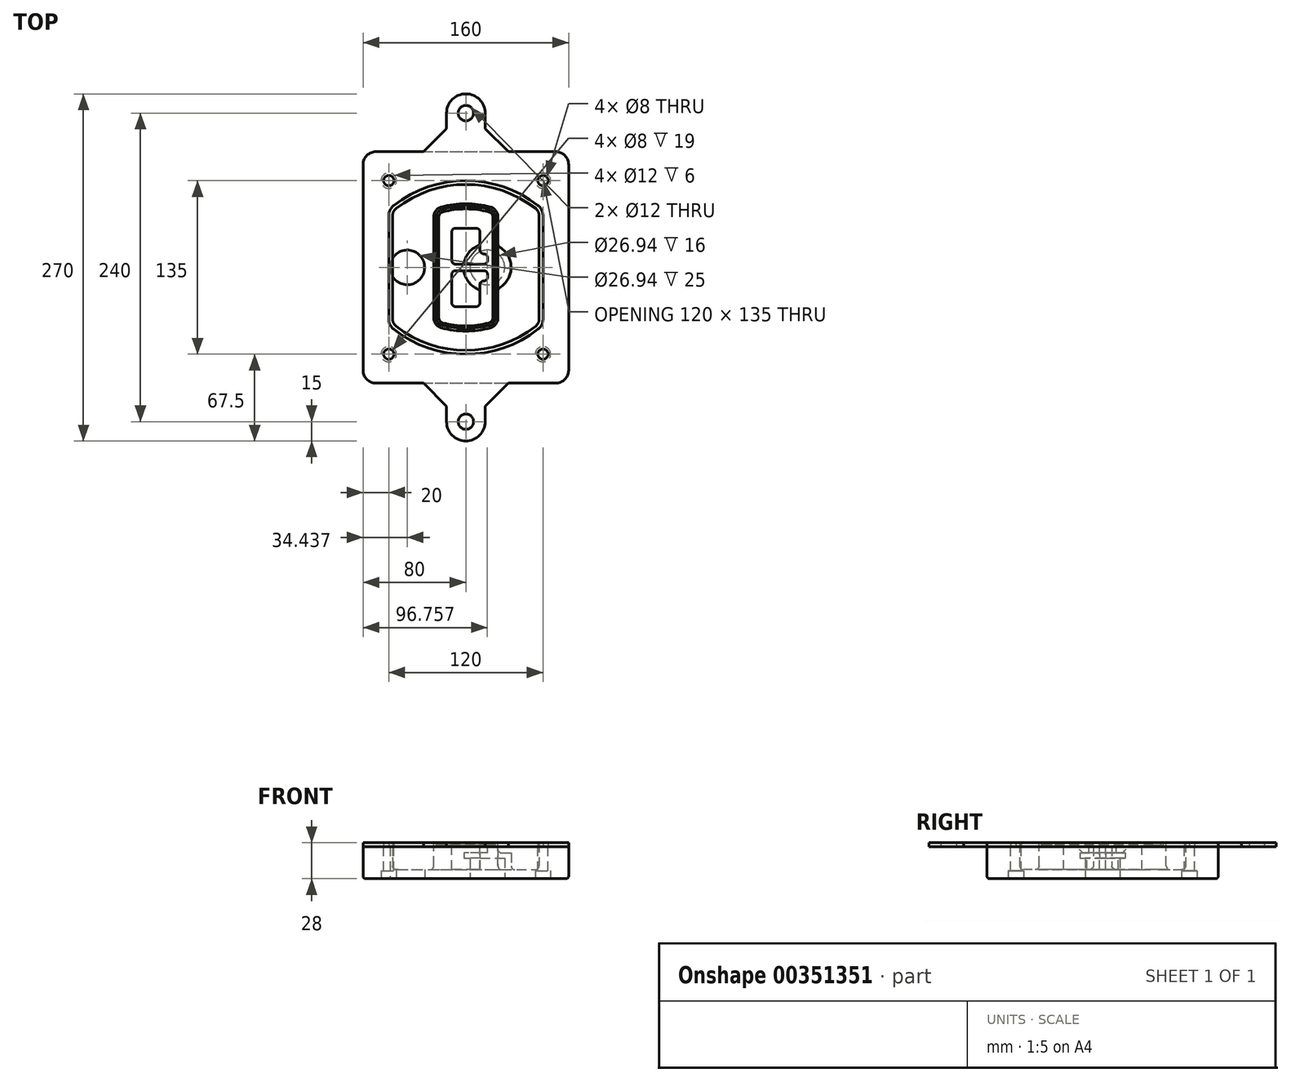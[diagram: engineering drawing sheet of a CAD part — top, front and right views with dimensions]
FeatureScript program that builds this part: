
annotation { "Feature Type Name" : "Feature", "Feature Type Description" : "" }
export const myFeature = defineFeature(function(context is Context, id is Id, definition is map)
    precondition{}
    {
        {
            var Q0;
            Q0=qCreatedBy(makeId("Top.planeOp"),FACE);
            var sketch = newSketch(context, id + "F0", { "sketchPlane" : qUnion([Q0])});
            skPoint(sketch, "E0.rect.middle", {"position": v(0, 0) * mm});
            skLineSegment(sketch, "E1.bottom", {"start": v(-70, -90) * mm, "end": v(70, -90) * mm});
            skLineSegment(sketch, "E1.top", {"start": v(-70, 90) * mm, "end": v(70, 90) * mm});
            skLineSegment(sketch, "E1.left", {"start": v(-80, -80) * mm, "end": v(-80, 80) * mm});
            skLineSegment(sketch, "E1.right", {"start": v(80, -80) * mm, "end": v(80, 80) * mm});
            skLineSegment(sketch, "E2", {"start": v(-80, 90) * mm, "end": v(80, -90) * mm, "construction": true});
            skLineSegment(sketch, "E3", {"start": v(80, 90) * mm, "end": v(-80, -90) * mm, "construction": true});
            skCircle(sketch, "E4", {"center": v(-60, 67.5) * mm, "radius": 4 * mm});
            skCircle(sketch, "E5", {"center": v(60, 67.5) * mm, "radius": 4 * mm});
            skCircle(sketch, "E6", {"center": v(60, -67.5) * mm, "radius": 4 * mm});
            skCircle(sketch, "E7", {"center": v(-60, -67.5) * mm, "radius": 4 * mm});
            skLineSegment(sketch, "E8", {"start": v(-60, 67.5) * mm, "end": v(60, 67.5) * mm, "construction": true});
            skLineSegment(sketch, "E9", {"start": v(60, 67.5) * mm, "end": v(60, -67.5) * mm, "construction": true});
            skLineSegment(sketch, "E10", {"start": v(60, -67.5) * mm, "end": v(-60, -67.5) * mm, "construction": true});
            skLineSegment(sketch, "E11", {"start": v(-60, -67.5) * mm, "end": v(-60, 67.5) * mm, "construction": true});
            skLineSegment(sketch, "E12", {"start": v(-60, 40.3) * mm, "end": v(-60, -40.3) * mm});
            skLineSegment(sketch, "E13", {"start": v(60, 40.3) * mm, "end": v(60, -40.3) * mm});
            skArc(sketch, "E14", {"start": v(56.15, 48.18) * mm, "mid": v(0, 67.5) * mm, "end": v(-56.15, 48.18) * mm});
            skArc(sketch, "E15", {"start": v(-56.15, -48.18) * mm, "mid": v(0, -67.5) * mm, "end": v(56.15, -48.18) * mm});
            skLineSegment(sketch, "E16", {"start": v(-60, 0) * mm, "end": v(60, 0) * mm, "construction": true});
            skPoint(sketch, "E17.visualSharp", {"position": v(-60, -45) * mm});
            skArc(sketch, "E17.filletArc", {"start": v(-60, -40.3) * mm, "mid": v(-58.99, -44.68) * mm, "end": v(-56.15, -48.18) * mm});
            skPoint(sketch, "E18.visualSharp", {"position": v(-60, 45) * mm});
            skArc(sketch, "E18.filletArc", {"start": v(-56.15, 48.18) * mm, "mid": v(-58.99, 44.68) * mm, "end": v(-60, 40.3) * mm});
            skPoint(sketch, "E19.visualSharp", {"position": v(60, 45) * mm});
            skArc(sketch, "E19.filletArc", {"start": v(60, 40.3) * mm, "mid": v(58.99, 44.68) * mm, "end": v(56.15, 48.18) * mm});
            skPoint(sketch, "E20.visualSharp", {"position": v(60, -45) * mm});
            skArc(sketch, "E20.filletArc", {"start": v(56.15, -48.18) * mm, "mid": v(58.99, -44.68) * mm, "end": v(60, -40.3) * mm});
            skPoint(sketch, "E21.visualSharp", {"position": v(-80, 90) * mm});
            skArc(sketch, "E21.filletArc", {"start": v(-70, 90) * mm, "mid": v(-77.07, 87.07) * mm, "end": v(-80, 80) * mm});
            skPoint(sketch, "E22.visualSharp", {"position": v(80, 90) * mm});
            skArc(sketch, "E22.filletArc", {"start": v(80, 80) * mm, "mid": v(77.07, 87.07) * mm, "end": v(70, 90) * mm});
            skPoint(sketch, "E23.visualSharp", {"position": v(80, -90) * mm});
            skArc(sketch, "E23.filletArc", {"start": v(70, -90) * mm, "mid": v(77.07, -87.07) * mm, "end": v(80, -80) * mm});
            skPoint(sketch, "E24.visualSharp", {"position": v(-80, -90) * mm});
            skArc(sketch, "E24.filletArc", {"start": v(-80, -80) * mm, "mid": v(-77.07, -87.07) * mm, "end": v(-70, -90) * mm});
            skArc(sketch, "E25.0", {"start": v(57, 40.3) * mm, "mid": v(56.3, 43.36) * mm, "end": v(54.3, 45.81) * mm});
            skLineSegment(sketch, "E25.1", {"start": v(57, 40.3) * mm, "end": v(57, -40.3) * mm});
            skArc(sketch, "E25.2", {"start": v(54.3, -45.81) * mm, "mid": v(56.3, -43.36) * mm, "end": v(57, -40.3) * mm});
            skArc(sketch, "E25.3", {"start": v(-54.3, -45.81) * mm, "mid": v(0, -64.5) * mm, "end": v(54.3, -45.81) * mm});
            skArc(sketch, "E25.4", {"start": v(-57, -40.3) * mm, "mid": v(-56.3, -43.36) * mm, "end": v(-54.3, -45.81) * mm});
            skArc(sketch, "E25.5", {"start": v(54.3, 45.81) * mm, "mid": v(0, 64.5) * mm, "end": v(-54.3, 45.81) * mm});
            skLineSegment(sketch, "E25.6", {"start": v(-57, 40.3) * mm, "end": v(-57, -40.3) * mm});
            skArc(sketch, "E25.7", {"start": v(-54.3, 45.81) * mm, "mid": v(-56.3, 43.36) * mm, "end": v(-57, 40.3) * mm});
            skArc(sketch, "E26.0", {"start": v(-58.62, 51.33) * mm, "mid": v(-62.58, 46.43) * mm, "end": v(-64, 40.3) * mm});
            skArc(sketch, "E26.1", {"start": v(58.62, 51.33) * mm, "mid": v(0, 71.5) * mm, "end": v(-58.62, 51.33) * mm});
            skArc(sketch, "E26.2", {"start": v(64, 40.3) * mm, "mid": v(62.58, 46.43) * mm, "end": v(58.62, 51.33) * mm});
            skLineSegment(sketch, "E26.3", {"start": v(64, 40.3) * mm, "end": v(64, -40.3) * mm});
            skArc(sketch, "E26.4", {"start": v(58.62, -51.33) * mm, "mid": v(62.58, -46.43) * mm, "end": v(64, -40.3) * mm});
            skLineSegment(sketch, "E26.5", {"start": v(-64, 40.3) * mm, "end": v(-64, -40.3) * mm});
            skArc(sketch, "E26.6", {"start": v(-58.62, -51.33) * mm, "mid": v(0, -71.5) * mm, "end": v(58.62, -51.33) * mm});
            skArc(sketch, "E26.7", {"start": v(-64, -40.3) * mm, "mid": v(-62.58, -46.43) * mm, "end": v(-58.62, -51.33) * mm});
            skSolve(sketch);
        }
        {
            var Q0;
            Q0=makeQuery(id+"F0.imprint","IMPRINT",FACE,{"disambiguationData":[TD([[makeQuery(id+"F0.imprint","IMPRINT",EDGE,{"derivedFrom":sQuery(id+"F0.wireOp",EDGE,"E1.bottom")}),1.0]])]});
            var Q1;
            Q1=makeQuery(id+"F0.imprint","IMPRINT",FACE,{"disambiguationData":[TD([[makeQuery(id+"F0.imprint","IMPRINT",EDGE,{"derivedFrom":sQuery(id+"F0.wireOp",EDGE,"E12")}),1.0]])]});
            var Q2;
            Q2=makeQuery(id+"F0.imprint","IMPRINT",FACE,{"disambiguationData":[TD([[makeQuery(id+"F0.imprint","IMPRINT",EDGE,{"derivedFrom":sQuery(id+"F0.wireOp",EDGE,"E25.0")}),1.0]])]});
            var Q3;
            Q3=makeQuery(id+"F0.imprint","IMPRINT",FACE,{"disambiguationData":[TD([[makeQuery(id+"F0.imprint","IMPRINT",EDGE,{"derivedFrom":sQuery(id+"F0.wireOp",EDGE,"E12")}),-1.0]])]});
            extrude(context, id + "F1", {"entities" : qUnion([Q0, Q1, Q2, Q3]), "oppositeDirection" : true, "depth" : 25 * mm});
        }
        {
            var Q0;
            Q0=makeQuery(id+"F0.imprint","IMPRINT",FACE,{"disambiguationData":[TD([[makeQuery(id+"F0.imprint","IMPRINT",EDGE,{"derivedFrom":sQuery(id+"F0.wireOp",EDGE,"E12")}),1.0]])]});
            extrude(context, id + "F2", {"entities" : qUnion([Q0]), "operationType" : NewBodyOperationType.ADD, "depth" : 3 * mm});
        }
        {
            var Q0;
            Q0=makeQuery(id+"F0.imprint","IMPRINT",FACE,{"disambiguationData":[TD([[makeQuery(id+"F0.imprint","IMPRINT",EDGE,{"derivedFrom":sQuery(id+"F0.wireOp",EDGE,"E25.0")}),1.0]])]});
            extrude(context, id + "F3", {"entities" : qUnion([Q0]), "operationType" : NewBodyOperationType.REMOVE, "oppositeDirection" : true, "depth" : 18 * mm});
        }
        {
            var Q0;
            Q0=makeQuery(id+"F2.opExtrude","CAP_FACE",FACE,{"disambiguationData":[OSD([sQuery(id+"F0.wireOp",EDGE,"E12"),sQuery(id+"F0.wireOp",EDGE,"E13"),sQuery(id+"F0.wireOp",EDGE,"E14"),sQuery(id+"F0.wireOp",EDGE,"E15"),sQuery(id+"F0.wireOp",EDGE,"E17.filletArc"),sQuery(id+"F0.wireOp",EDGE,"E18.filletArc"),sQuery(id+"F0.wireOp",EDGE,"E19.filletArc"),sQuery(id+"F0.wireOp",EDGE,"E20.filletArc"),sQuery(id+"F0.wireOp",EDGE,"E25.0"),sQuery(id+"F0.wireOp",EDGE,"E25.1"),sQuery(id+"F0.wireOp",EDGE,"E25.2"),sQuery(id+"F0.wireOp",EDGE,"E25.3"),sQuery(id+"F0.wireOp",EDGE,"E25.4"),sQuery(id+"F0.wireOp",EDGE,"E25.5"),sQuery(id+"F0.wireOp",EDGE,"E25.6"),sQuery(id+"F0.wireOp",EDGE,"E25.7")])],"isStart":false});
            var sketch = newSketch(context, id + "F4", { "sketchPlane" : qUnion([Q0])});
            skArc(sketch, "E27.0", {"start": v(-19.08, -46.97) * mm, "mid": v(0, -49.5) * mm, "end": v(19.08, -46.97) * mm});
            skArc(sketch, "E28.0", {"start": v(19.08, 46.97) * mm, "mid": v(0, 49.5) * mm, "end": v(-19.08, 46.97) * mm});
            skLineSegment(sketch, "E29", {"start": v(-25, 39.25) * mm, "end": v(-25, -39.25) * mm});
            skLineSegment(sketch, "E30", {"start": v(25, 39.25) * mm, "end": v(25, -39.25) * mm});
            skLineSegment(sketch, "E31", {"start": v(-25, 45.1) * mm, "end": v(25, 45.1) * mm, "construction": true});
            skLineSegment(sketch, "E32", {"start": v(-25, -45.1) * mm, "end": v(25, -45.1) * mm, "construction": true});
            skPoint(sketch, "E33.visualSharp", {"position": v(-25, 45.1) * mm});
            skArc(sketch, "E33.filletArc", {"start": v(-19.08, 46.97) * mm, "mid": v(-23.35, 44.11) * mm, "end": v(-25, 39.25) * mm});
            skPoint(sketch, "E34.visualSharp", {"position": v(25, 45.1) * mm});
            skArc(sketch, "E34.filletArc", {"start": v(25, 39.25) * mm, "mid": v(23.35, 44.11) * mm, "end": v(19.08, 46.97) * mm});
            skPoint(sketch, "E35.visualSharp", {"position": v(25, -45.1) * mm});
            skArc(sketch, "E35.filletArc", {"start": v(19.08, -46.97) * mm, "mid": v(23.35, -44.11) * mm, "end": v(25, -39.25) * mm});
            skPoint(sketch, "E36.visualSharp", {"position": v(-25, -45.1) * mm});
            skArc(sketch, "E36.filletArc", {"start": v(-25, -39.25) * mm, "mid": v(-23.35, -44.11) * mm, "end": v(-19.08, -46.97) * mm});
            skArc(sketch, "E37.0", {"start": v(54.3, 45.81) * mm, "mid": v(0, 64.5) * mm, "end": v(-54.3, 45.81) * mm});
            skArc(sketch, "E37.1", {"start": v(-54.3, 45.81) * mm, "mid": v(-56.3, 43.36) * mm, "end": v(-57, 40.3) * mm});
            skLineSegment(sketch, "E37.2", {"start": v(-57, 40.3) * mm, "end": v(-57, -40.3) * mm});
            skArc(sketch, "E37.3", {"start": v(-57, -40.3) * mm, "mid": v(-56.3, -43.36) * mm, "end": v(-54.3, -45.81) * mm});
            skArc(sketch, "E37.4", {"start": v(-54.3, -45.81) * mm, "mid": v(0, -64.5) * mm, "end": v(54.3, -45.81) * mm});
            skArc(sketch, "E37.5", {"start": v(54.3, -45.81) * mm, "mid": v(56.3, -43.36) * mm, "end": v(57, -40.3) * mm});
            skLineSegment(sketch, "E37.6", {"start": v(57, 40.3) * mm, "end": v(57, -40.3) * mm});
            skArc(sketch, "E37.7", {"start": v(57, 40.3) * mm, "mid": v(56.3, 43.36) * mm, "end": v(54.3, 45.81) * mm});
            skLineSegment(sketch, "E38.0", {"start": v(23, 39.25) * mm, "end": v(23, -39.25) * mm});
            skArc(sketch, "E38.1", {"start": v(18.56, -45.04) * mm, "mid": v(21.76, -42.9) * mm, "end": v(23, -39.25) * mm});
            skArc(sketch, "E38.2", {"start": v(-18.56, -45.04) * mm, "mid": v(0, -47.5) * mm, "end": v(18.56, -45.04) * mm});
            skArc(sketch, "E38.3", {"start": v(-23, -39.25) * mm, "mid": v(-21.76, -42.9) * mm, "end": v(-18.56, -45.04) * mm});
            skLineSegment(sketch, "E38.4", {"start": v(-23, 39.25) * mm, "end": v(-23, -39.25) * mm});
            skArc(sketch, "E38.5", {"start": v(23, 39.25) * mm, "mid": v(21.76, 42.9) * mm, "end": v(18.56, 45.04) * mm});
            skArc(sketch, "E38.6", {"start": v(-18.56, 45.04) * mm, "mid": v(-21.76, 42.9) * mm, "end": v(-23, 39.25) * mm});
            skArc(sketch, "E38.7", {"start": v(18.56, 45.04) * mm, "mid": v(0, 47.5) * mm, "end": v(-18.56, 45.04) * mm});
            skArc(sketch, "E39.0", {"start": v(21, 39.25) * mm, "mid": v(20.18, 41.68) * mm, "end": v(18.04, 43.1) * mm});
            skLineSegment(sketch, "E39.1", {"start": v(21, 39.25) * mm, "end": v(21, -39.25) * mm});
            skArc(sketch, "E39.2", {"start": v(18.04, -43.1) * mm, "mid": v(20.18, -41.68) * mm, "end": v(21, -39.25) * mm});
            skArc(sketch, "E39.3", {"start": v(-18.04, -43.1) * mm, "mid": v(0, -45.5) * mm, "end": v(18.04, -43.1) * mm});
            skArc(sketch, "E39.4", {"start": v(-21, -39.25) * mm, "mid": v(-20.18, -41.68) * mm, "end": v(-18.04, -43.1) * mm});
            skArc(sketch, "E39.5", {"start": v(18.04, 43.1) * mm, "mid": v(0, 45.5) * mm, "end": v(-18.04, 43.1) * mm});
            skLineSegment(sketch, "E39.6", {"start": v(-21, 39.25) * mm, "end": v(-21, -39.25) * mm});
            skArc(sketch, "E39.7", {"start": v(-18.04, 43.1) * mm, "mid": v(-20.18, 41.68) * mm, "end": v(-21, 39.25) * mm});
            skLineSegment(sketch, "E40", {"start": v(-25, 0) * mm, "end": v(25, 0) * mm, "construction": true});
            skLineSegment(sketch, "E41", {"start": v(-11, 5.5) * mm, "end": v(-11, 27.5) * mm});
            skLineSegment(sketch, "E42", {"start": v(-8, 30.5) * mm, "end": v(8, 30.5) * mm});
            skLineSegment(sketch, "E43", {"start": v(11, 27.5) * mm, "end": v(11, 13.5) * mm});
            skLineSegment(sketch, "E44", {"start": v(14, 10.5) * mm, "end": v(14, 10.5) * mm});
            skLineSegment(sketch, "E45", {"start": v(17, 7.5) * mm, "end": v(17, 5.5) * mm});
            skLineSegment(sketch, "E46", {"start": v(14, 2.5) * mm, "end": v(-8, 2.5) * mm});
            skPoint(sketch, "E47.visualSharp", {"position": v(-11, 30.5) * mm});
            skArc(sketch, "E47.filletArc", {"start": v(-8, 30.5) * mm, "mid": v(-10.12, 29.62) * mm, "end": v(-11, 27.5) * mm});
            skPoint(sketch, "E48.visualSharp", {"position": v(11, 30.5) * mm});
            skArc(sketch, "E48.filletArc", {"start": v(11, 27.5) * mm, "mid": v(10.12, 29.62) * mm, "end": v(8, 30.5) * mm});
            skPoint(sketch, "E49.visualSharp", {"position": v(11, 10.5) * mm});
            skArc(sketch, "E49.filletArc", {"start": v(11, 13.5) * mm, "mid": v(11.88, 11.38) * mm, "end": v(14, 10.5) * mm});
            skPoint(sketch, "E50.visualSharp", {"position": v(17, 10.5) * mm});
            skArc(sketch, "E50.filletArc", {"start": v(17, 7.5) * mm, "mid": v(16.12, 9.62) * mm, "end": v(14, 10.5) * mm});
            skPoint(sketch, "E51.visualSharp", {"position": v(17, 2.5) * mm});
            skArc(sketch, "E51.filletArc", {"start": v(14, 2.5) * mm, "mid": v(16.12, 3.38) * mm, "end": v(17, 5.5) * mm});
            skPoint(sketch, "E52.visualSharp", {"position": v(-11, 2.5) * mm});
            skArc(sketch, "E52.filletArc", {"start": v(-11, 5.5) * mm, "mid": v(-10.12, 3.38) * mm, "end": v(-8, 2.5) * mm});
            skLineSegment(sketch, "E53.0.MirrorCS", {"start": v(14, -2.5) * mm, "end": v(-8, -2.5) * mm});
            skArc(sketch, "E54.0.MirrorCS", {"start": v(-11, -5.5) * mm, "mid": v(-10.12, -3.38) * mm, "end": v(-8, -2.5) * mm});
            skLineSegment(sketch, "E55.0.MirrorCS", {"start": v(-11, -5.5) * mm, "end": v(-11, -27.5) * mm});
            skArc(sketch, "E56.0.MirrorCS", {"start": v(-8, -30.5) * mm, "mid": v(-10.12, -29.62) * mm, "end": v(-11, -27.5) * mm});
            skLineSegment(sketch, "E57.0.MirrorCS", {"start": v(-8, -30.5) * mm, "end": v(8, -30.5) * mm});
            skArc(sketch, "E58.0.MirrorCS", {"start": v(11, -27.5) * mm, "mid": v(10.12, -29.62) * mm, "end": v(8, -30.5) * mm});
            skLineSegment(sketch, "E59.0.MirrorCS", {"start": v(11, -27.5) * mm, "end": v(11, -13.5) * mm});
            skArc(sketch, "E60.0.MirrorCS", {"start": v(11, -13.5) * mm, "mid": v(11.88, -11.38) * mm, "end": v(14, -10.5) * mm});
            skArc(sketch, "E61.0.MirrorCS", {"start": v(17, -7.5) * mm, "mid": v(16.12, -9.62) * mm, "end": v(14, -10.5) * mm});
            skLineSegment(sketch, "E62.0.MirrorCS", {"start": v(17, -7.5) * mm, "end": v(17, -5.5) * mm});
            skArc(sketch, "E63.0.MirrorCS", {"start": v(14, -2.5) * mm, "mid": v(16.12, -3.38) * mm, "end": v(17, -5.5) * mm});
            skSolve(sketch);
        }
        {
            var Q0;
            Q0=makeQuery(id+"F4.imprint","IMPRINT",FACE,{"disambiguationData":[TD([[makeQuery(id+"F4.imprint","IMPRINT",EDGE,{"derivedFrom":sQuery(id+"F4.wireOp",EDGE,"E27.0")}),1.0]])]});
            var Q1;
            Q1=makeQuery(id+"F4.imprint","IMPRINT",FACE,{"disambiguationData":[TD([[makeQuery(id+"F4.imprint","IMPRINT",EDGE,{"derivedFrom":sQuery(id+"F4.wireOp",EDGE,"E38.0")}),-1.0]])]});
            var Q2;
            Q2=makeQuery(id+"F4.imprint","IMPRINT",FACE,{"disambiguationData":[TD([[makeQuery(id+"F4.imprint","IMPRINT",EDGE,{"derivedFrom":sQuery(id+"F4.wireOp",EDGE,"E39.0")}),1.0]])]});
            extrude(context, id + "F5", {"entities" : qUnion([Q0, Q1, Q2]), "operationType" : NewBodyOperationType.ADD, "endBound" : BoundingType.UP_TO_NEXT, "oppositeDirection" : true, "depth" : 25 * mm});
        }
        {
            var Q0;
            Q0=makeQuery(id+"F4.imprint","IMPRINT",FACE,{"disambiguationData":[TD([[makeQuery(id+"F4.imprint","IMPRINT",EDGE,{"derivedFrom":sQuery(id+"F4.wireOp",EDGE,"E38.0")}),-1.0]])]});
            extrude(context, id + "F6", {"entities" : qUnion([Q0]), "operationType" : NewBodyOperationType.REMOVE, "oppositeDirection" : true, "depth" : 2 * mm});
        }
        {
            var Q0;
            Q0=makeQuery(id+"F1.opExtrude","CAP_FACE",FACE,{"disambiguationData":[OSD([sQuery(id+"F0.wireOp",EDGE,"E1.bottom"),sQuery(id+"F0.wireOp",EDGE,"E1.top"),sQuery(id+"F0.wireOp",EDGE,"E1.left"),sQuery(id+"F0.wireOp",EDGE,"E1.right"),sQuery(id+"F0.wireOp",EDGE,"E4"),sQuery(id+"F0.wireOp",EDGE,"E5"),sQuery(id+"F0.wireOp",EDGE,"E6"),sQuery(id+"F0.wireOp",EDGE,"E7"),sQuery(id+"F0.wireOp",EDGE,"E21.filletArc"),sQuery(id+"F0.wireOp",EDGE,"E22.filletArc"),sQuery(id+"F0.wireOp",EDGE,"E23.filletArc"),sQuery(id+"F0.wireOp",EDGE,"E24.filletArc")])],"isStart":false});
            var sketch = newSketch(context, id + "F7", { "sketchPlane" : qUnion([Q0])});
            skCircle(sketch, "E64", {"center": v(16.76, 0) * mm, "radius": 13.47 * mm});
            skCircle(sketch, "E65", {"center": v(-45.56, 0) * mm, "radius": 13.47 * mm});
            skLineSegment(sketch, "E66", {"start": v(80, 0) * mm, "end": v(-80, 0) * mm});
            skCircle(sketch, "E67", {"center": v(16.76, 0) * mm, "radius": 18.47 * mm});
            skCircle(sketch, "E68", {"center": v(60, -67.5) * mm, "radius": 6 * mm});
            skCircle(sketch, "E69", {"center": v(-60, -67.5) * mm, "radius": 6 * mm});
            skCircle(sketch, "E70", {"center": v(-60, 67.5) * mm, "radius": 6 * mm});
            skCircle(sketch, "E71", {"center": v(60, 67.5) * mm, "radius": 6 * mm});
            skSolve(sketch);
        }
        {
            var Q0;
            {var subQ1=sQuery(id+"F7.wireOp",EDGE,"E66");var subQ4=sQuery(id+"F7.wireOp",EDGE,"E64");var subQ6=makeQuery(id+"F7.imprint","INTERSECT",VERTEX,{"disambiguationData":[OD(0.0)],"derivedFrom":[subQ4,subQ1]});Q0=makeQuery(id+"F7.imprint","IMPRINT",FACE,{"disambiguationData":[TD([[makeQuery(id+"F7.imprint","IMPRINT",EDGE,{"disambiguationData":[TD([[subQ6,-1.0]])],"derivedFrom":subQ4}),-1.0]])]});}
            var Q1;
            {var subQ0=sQuery(id+"F7.wireOp",EDGE,"E66");var subQ1=sQuery(id+"F7.wireOp",EDGE,"E64");var subQ3=makeQuery(id+"F7.imprint","INTERSECT",VERTEX,{"disambiguationData":[OD(0.0)],"derivedFrom":[subQ1,subQ0]});Q1=makeQuery(id+"F7.imprint","IMPRINT",FACE,{"disambiguationData":[TD([[makeQuery(id+"F7.imprint","IMPRINT",EDGE,{"disambiguationData":[TD([[subQ3,-1.0]])],"derivedFrom":subQ1}),1.0]])]});}
            var Q2;
            {var subQ0=sQuery(id+"F7.wireOp",EDGE,"E66");var subQ1=sQuery(id+"F7.wireOp",EDGE,"E64");var subQ3=makeQuery(id+"F7.imprint","INTERSECT",VERTEX,{"disambiguationData":[OD(0.0)],"derivedFrom":[subQ1,subQ0]});Q2=makeQuery(id+"F7.imprint","IMPRINT",FACE,{"disambiguationData":[TD([[makeQuery(id+"F7.imprint","IMPRINT",EDGE,{"disambiguationData":[TD([[subQ3,1.0]])],"derivedFrom":subQ1}),1.0]])]});}
            var Q3;
            {var subQ1=sQuery(id+"F7.wireOp",EDGE,"E66");var subQ4=sQuery(id+"F7.wireOp",EDGE,"E64");var subQ6=makeQuery(id+"F7.imprint","INTERSECT",VERTEX,{"disambiguationData":[OD(0.0)],"derivedFrom":[subQ4,subQ1]});Q3=makeQuery(id+"F7.imprint","IMPRINT",FACE,{"disambiguationData":[TD([[makeQuery(id+"F7.imprint","IMPRINT",EDGE,{"disambiguationData":[TD([[subQ6,1.0]])],"derivedFrom":subQ4}),-1.0]])]});}
            extrude(context, id + "F8", {"entities" : qUnion([Q0, Q1, Q2, Q3]), "operationType" : NewBodyOperationType.ADD, "oppositeDirection" : true, "depth" : 20 * mm});
        }
        {
            var Q0;
            {var subQ0=sQuery(id+"F7.wireOp",EDGE,"E66");var subQ1=sQuery(id+"F7.wireOp",EDGE,"E64");var subQ3=makeQuery(id+"F7.imprint","INTERSECT",VERTEX,{"disambiguationData":[OD(0.0)],"derivedFrom":[subQ1,subQ0]});Q0=makeQuery(id+"F7.imprint","IMPRINT",FACE,{"disambiguationData":[TD([[makeQuery(id+"F7.imprint","IMPRINT",EDGE,{"disambiguationData":[TD([[subQ3,-1.0]])],"derivedFrom":subQ1}),1.0]])]});}
            var Q1;
            {var subQ0=sQuery(id+"F7.wireOp",EDGE,"E66");var subQ1=sQuery(id+"F7.wireOp",EDGE,"E64");var subQ3=makeQuery(id+"F7.imprint","INTERSECT",VERTEX,{"disambiguationData":[OD(0.0)],"derivedFrom":[subQ1,subQ0]});Q1=makeQuery(id+"F7.imprint","IMPRINT",FACE,{"disambiguationData":[TD([[makeQuery(id+"F7.imprint","IMPRINT",EDGE,{"disambiguationData":[TD([[subQ3,1.0]])],"derivedFrom":subQ1}),1.0]])]});}
            extrude(context, id + "F9", {"entities" : qUnion([Q0, Q1]), "operationType" : NewBodyOperationType.REMOVE, "oppositeDirection" : true, "depth" : 16 * mm});
        }
        {
            var Q0;
            {var subQ0=sQuery(id+"F7.wireOp",EDGE,"E66");var subQ1=sQuery(id+"F7.wireOp",EDGE,"E65");var subQ3=makeQuery(id+"F7.imprint","INTERSECT",VERTEX,{"disambiguationData":[OD(0.0)],"derivedFrom":[subQ1,subQ0]});Q0=makeQuery(id+"F7.imprint","IMPRINT",FACE,{"disambiguationData":[TD([[makeQuery(id+"F7.imprint","IMPRINT",EDGE,{"disambiguationData":[TD([[subQ3,-1.0]])],"derivedFrom":subQ1}),1.0]])]});}
            var Q1;
            {var subQ0=sQuery(id+"F7.wireOp",EDGE,"E66");var subQ1=sQuery(id+"F7.wireOp",EDGE,"E65");var subQ3=makeQuery(id+"F7.imprint","INTERSECT",VERTEX,{"disambiguationData":[OD(0.0)],"derivedFrom":[subQ1,subQ0]});Q1=makeQuery(id+"F7.imprint","IMPRINT",FACE,{"disambiguationData":[TD([[makeQuery(id+"F7.imprint","IMPRINT",EDGE,{"disambiguationData":[TD([[subQ3,1.0]])],"derivedFrom":subQ1}),1.0]])]});}
            extrude(context, id + "F10", {"entities" : qUnion([Q0, Q1]), "operationType" : NewBodyOperationType.REMOVE, "oppositeDirection" : true, "depth" : 25 * mm});
        }
        {
            var Q0;
            Q0=makeQuery(id+"F7.imprint","IMPRINT",FACE,{"disambiguationData":[TD([[makeQuery(id+"F7.imprint","IMPRINT",EDGE,{"derivedFrom":sQuery(id+"F7.wireOp",EDGE,"E68")}),1.0]])]});
            var Q1;
            Q1=makeQuery(id+"F7.imprint","IMPRINT",FACE,{"disambiguationData":[TD([[makeQuery(id+"F7.imprint","IMPRINT",EDGE,{"derivedFrom":makeQuery(id+"F1.opExtrude","CAP_EDGE",EDGE,{"disambiguationData":[OSD([sQuery(id+"F0.wireOp",EDGE,"E5")])],"isStart":false})}),-1.0]])]});
            var Q2;
            Q2=makeQuery(id+"F7.imprint","IMPRINT",FACE,{"disambiguationData":[TD([[makeQuery(id+"F7.imprint","IMPRINT",EDGE,{"derivedFrom":sQuery(id+"F7.wireOp",EDGE,"E69")}),1.0]])]});
            var Q3;
            Q3=makeQuery(id+"F7.imprint","IMPRINT",FACE,{"disambiguationData":[TD([[makeQuery(id+"F7.imprint","IMPRINT",EDGE,{"derivedFrom":makeQuery(id+"F1.opExtrude","CAP_EDGE",EDGE,{"disambiguationData":[OSD([sQuery(id+"F0.wireOp",EDGE,"E4")])],"isStart":false})}),-1.0]])]});
            var Q4;
            Q4=makeQuery(id+"F7.imprint","IMPRINT",FACE,{"disambiguationData":[TD([[makeQuery(id+"F7.imprint","IMPRINT",EDGE,{"derivedFrom":sQuery(id+"F7.wireOp",EDGE,"E70")}),1.0]])]});
            var Q5;
            Q5=makeQuery(id+"F7.imprint","IMPRINT",FACE,{"disambiguationData":[TD([[makeQuery(id+"F7.imprint","IMPRINT",EDGE,{"derivedFrom":makeQuery(id+"F1.opExtrude","CAP_EDGE",EDGE,{"disambiguationData":[OSD([sQuery(id+"F0.wireOp",EDGE,"E7")])],"isStart":false})}),-1.0]])]});
            var Q6;
            Q6=makeQuery(id+"F7.imprint","IMPRINT",FACE,{"disambiguationData":[TD([[makeQuery(id+"F7.imprint","IMPRINT",EDGE,{"derivedFrom":sQuery(id+"F7.wireOp",EDGE,"E71")}),1.0]])]});
            var Q7;
            Q7=makeQuery(id+"F7.imprint","IMPRINT",FACE,{"disambiguationData":[TD([[makeQuery(id+"F7.imprint","IMPRINT",EDGE,{"derivedFrom":makeQuery(id+"F1.opExtrude","CAP_EDGE",EDGE,{"disambiguationData":[OSD([sQuery(id+"F0.wireOp",EDGE,"E6")])],"isStart":false})}),-1.0]])]});
            extrude(context, id + "F11", {"entities" : qUnion([Q0, Q1, Q2, Q3, Q4, Q5, Q6, Q7]), "operationType" : NewBodyOperationType.REMOVE, "oppositeDirection" : true, "depth" : 6 * mm});
        }
        {
            var Q0;
            Q0=makeQuery(id+"F9.boolean.opBoolean","COPY",FACE,{"derivedFrom":makeQuery(id+"F9.opExtrude","CAP_FACE",FACE,{"disambiguationData":[OSD([sQuery(id+"F7.wireOp",EDGE,"E64")])],"isStart":false})});
            var sketch = newSketch(context, id + "F12", { "sketchPlane" : qUnion([Q0])});
            skArc(sketch, "E72.0", {"start": v(11, 17.55) * mm, "mid": v(2.57, 11.82) * mm, "end": v(-1.54, 2.5) * mm});
            skArc(sketch, "E72.1", {"start": v(-1.54, -2.5) * mm, "mid": v(2.57, -11.82) * mm, "end": v(11, -17.55) * mm});
            skLineSegment(sketch, "E73", {"start": v(-1.54, -2.5) * mm, "end": v(14, -2.5) * mm});
            skLineSegment(sketch, "E74.0", {"start": v(14, 2.5) * mm, "end": v(-1.54, 2.5) * mm});
            skArc(sketch, "E74.1", {"start": v(14, 2.5) * mm, "mid": v(16.12, 3.38) * mm, "end": v(17, 5.5) * mm});
            skLineSegment(sketch, "E74.2", {"start": v(17, 7.5) * mm, "end": v(17, 5.5) * mm});
            skArc(sketch, "E74.3", {"start": v(17, 7.5) * mm, "mid": v(16.12, 9.62) * mm, "end": v(14, 10.5) * mm});
            skArc(sketch, "E74.4", {"start": v(11, 13.5) * mm, "mid": v(11.88, 11.38) * mm, "end": v(14, 10.5) * mm});
            skLineSegment(sketch, "E74.5", {"start": v(11, 17.55) * mm, "end": v(11, 13.5) * mm});
            skLineSegment(sketch, "E74.7", {"start": v(14, -2.5) * mm, "end": v(-1.54, -2.5) * mm});
            skArc(sketch, "E74.8", {"start": v(14, -2.5) * mm, "mid": v(16.12, -3.38) * mm, "end": v(17, -5.5) * mm});
            skLineSegment(sketch, "E74.9", {"start": v(17, -7.5) * mm, "end": v(17, -5.5) * mm});
            skArc(sketch, "E74.10", {"start": v(17, -7.5) * mm, "mid": v(16.12, -9.62) * mm, "end": v(14, -10.5) * mm});
            skArc(sketch, "E74.11", {"start": v(11, -13.5) * mm, "mid": v(11.88, -11.38) * mm, "end": v(14, -10.5) * mm});
            skLineSegment(sketch, "E74.12", {"start": v(11, -17.55) * mm, "end": v(11, -13.5) * mm});
            skPoint(sketch, "E75.orphan", {"position": v(11, -27.5) * mm});
            skPoint(sketch, "E76.orphan", {"position": v(-8, -2.5) * mm});
            skPoint(sketch, "E77.orphan", {"position": v(-8, 2.5) * mm});
            skPoint(sketch, "E78.orphan", {"position": v(11, 27.5) * mm});
            skSolve(sketch);
        }
        {
            var Q0;
            {var subQ7=sQuery(id+"F12.wireOp",EDGE,"E72.0");var subQ14=sQuery(id+"F12.wireOp",EDGE,"E72.1");var subQ16=sQuery(id+"F12.wireOp",EDGE,"E74.1");var subQ18=sQuery(id+"F12.wireOp",EDGE,"E74.8");Q0=qUnion([makeQuery(id+"F12.imprint","IMPRINT",FACE,{"disambiguationData":[TD([[makeQuery(id+"F12.imprint","IMPRINT",EDGE,{"derivedFrom":subQ7}),1.0]])]}),makeQuery(id+"F12.imprint","IMPRINT",FACE,{"disambiguationData":[TD([[makeQuery(id+"F12.imprint","IMPRINT",EDGE,{"derivedFrom":subQ14}),1.0]])]}),makeQuery(id+"F12.imprint","IMPRINT",FACE,{"disambiguationData":[TD([[makeQuery(id+"F12.imprint","IMPRINT",EDGE,{"derivedFrom":subQ16}),1.0]])]}),makeQuery(id+"F12.imprint","IMPRINT",FACE,{"disambiguationData":[TD([[makeQuery(id+"F12.imprint","IMPRINT",EDGE,{"derivedFrom":subQ18}),-1.0]])]})]);}
            var Q1;
            Q1=makeQuery(id+"F5.boolean.opBoolean","SPLIT",FACE,{"disambiguationData":[TD([makeQuery(id+"F5.opExtrude","SWEPT_FACE",FACE,{"disambiguationData":[OSD([sQuery(id+"F4.wireOp",EDGE,"E41")])]})])],"derivedFrom":makeQuery(id+"F3.boolean.opBoolean","COPY",FACE,{"derivedFrom":makeQuery(id+"F3.opExtrude","CAP_FACE",FACE,{"disambiguationData":[OSD([sQuery(id+"F0.wireOp",EDGE,"E25.0"),sQuery(id+"F0.wireOp",EDGE,"E25.1"),sQuery(id+"F0.wireOp",EDGE,"E25.2"),sQuery(id+"F0.wireOp",EDGE,"E25.3"),sQuery(id+"F0.wireOp",EDGE,"E25.4"),sQuery(id+"F0.wireOp",EDGE,"E25.5"),sQuery(id+"F0.wireOp",EDGE,"E25.6"),sQuery(id+"F0.wireOp",EDGE,"E25.7")])],"isStart":false})})});
            extrude(context, id + "F13", {"entities" : qUnion([Q0]), "operationType" : NewBodyOperationType.REMOVE, "endBound" : BoundingType.UP_TO_SURFACE, "endBoundEntityFace" : qUnion([Q1]), "depth" : 25 * mm});
        }
        {
            var Q0;
            Q0=makeQuery(id+"F3.boolean.opBoolean","COPY",EDGE,{"derivedFrom":makeQuery(id+"F3.opExtrude","CAP_EDGE",EDGE,{"disambiguationData":[OSD([sQuery(id+"F0.wireOp",EDGE,"E25.6")])],"isStart":false})});
            var Q1;
            Q1=makeQuery(id+"F8.boolean.opBoolean","INTERSECT",EDGE,{"derivedFrom":[makeQuery(id+"F5.opExtrude","SWEPT_FACE",FACE,{"disambiguationData":[OSD([sQuery(id+"F4.wireOp",EDGE,"E30")])]}),makeQuery(id+"F8.opExtrude","CAP_FACE",FACE,{"disambiguationData":[OSD([sQuery(id+"F7.wireOp",EDGE,"E67")])],"isStart":false})]});
            var Q2;
            Q2=makeQuery(id+"F8.boolean.opBoolean","INTERSECT",EDGE,{"disambiguationData":[OD(1.0)],"derivedFrom":[makeQuery(id+"F5.opExtrude","SWEPT_FACE",FACE,{"disambiguationData":[OSD([sQuery(id+"F4.wireOp",EDGE,"E30")])]}),makeQuery(id+"F8.opExtrude","SWEPT_FACE",FACE,{"disambiguationData":[OSD([sQuery(id+"F7.wireOp",EDGE,"E67")])]})]});
            var Q3;
            {var subQ0=sQuery(id+"F4.wireOp",EDGE,"E30");Q3=makeQuery(id+"F8.boolean.opBoolean","SPLIT",EDGE,{"disambiguationData":[TD([makeQuery(id+"F5.opExtrude","SWEPT_FACE",FACE,{"disambiguationData":[OSD([sQuery(id+"F4.wireOp",EDGE,"E35.filletArc")])]})])],"derivedFrom":makeQuery(id+"F5.opExtrude","CAP_EDGE",EDGE,{"disambiguationData":[OSD([subQ0])],"isStart":false})});}
            var Q4;
            {var subQ0=sQuery(id+"F0.wireOp",EDGE,"E25.7");var subQ1=sQuery(id+"F0.wireOp",EDGE,"E25.1");var subQ2=sQuery(id+"F0.wireOp",EDGE,"E25.6");var subQ3=sQuery(id+"F0.wireOp",EDGE,"E25.5");var subQ4=sQuery(id+"F0.wireOp",EDGE,"E25.4");var subQ5=sQuery(id+"F0.wireOp",EDGE,"E25.0");var subQ6=sQuery(id+"F0.wireOp",EDGE,"E25.2");var subQ7=sQuery(id+"F0.wireOp",EDGE,"E25.3");Q4=makeQuery(id+"F8.boolean.opBoolean","INTERSECT",EDGE,{"derivedFrom":[makeQuery(id+"F5.boolean.opBoolean","SPLIT",FACE,{"disambiguationData":[TD([makeQuery(id+"F2.opExtrude","SWEPT_FACE",FACE,{"disambiguationData":[OSD([subQ5])]})])],"derivedFrom":makeQuery(id+"F3.boolean.opBoolean","COPY",FACE,{"derivedFrom":makeQuery(id+"F3.opExtrude","CAP_FACE",FACE,{"disambiguationData":[OSD([subQ5,subQ1,subQ6,subQ7,subQ4,subQ3,subQ2,subQ0])],"isStart":false})})}),makeQuery(id+"F8.opExtrude","SWEPT_FACE",FACE,{"disambiguationData":[OSD([sQuery(id+"F7.wireOp",EDGE,"E67")])]})]});}
            var Q5;
            Q5=makeQuery(id+"F8.boolean.opBoolean","INTERSECT",EDGE,{"disambiguationData":[OD(0.0)],"derivedFrom":[makeQuery(id+"F5.opExtrude","SWEPT_FACE",FACE,{"disambiguationData":[OSD([sQuery(id+"F4.wireOp",EDGE,"E30")])]}),makeQuery(id+"F8.opExtrude","SWEPT_FACE",FACE,{"disambiguationData":[OSD([sQuery(id+"F7.wireOp",EDGE,"E67")])]})]});
            fillet(context, id + "F14", {"entities" : qUnion([Q0, Q1, Q2, Q3, Q4, Q5]), "radius" : 3 * mm, "tangentPropagation" : true, "allowEdgeOverflow" : false});
        }
        {
            var Q0;
            Q0=makeQuery(id+"F1.opExtrude","CAP_EDGE",EDGE,{"disambiguationData":[OSD([sQuery(id+"F0.wireOp",EDGE,"E1.bottom")])],"isStart":false});
            fillet(context, id + "F15", {"entities" : qUnion([Q0]), "radius" : 2 * mm, "tangentPropagation" : true, "allowEdgeOverflow" : false});
        }
        {
            var Q0;
            {var subQ0=sQuery(id+"F0.wireOp",EDGE,"E21.filletArc");var subQ1=sQuery(id+"F0.wireOp",EDGE,"E7");var subQ2=sQuery(id+"F0.wireOp",EDGE,"E6");var subQ3=sQuery(id+"F0.wireOp",EDGE,"E5");var subQ4=sQuery(id+"F0.wireOp",EDGE,"E4");var subQ5=sQuery(id+"F0.wireOp",EDGE,"E22.filletArc");var subQ6=sQuery(id+"F0.wireOp",EDGE,"E1.bottom");var subQ7=sQuery(id+"F0.wireOp",EDGE,"E1.right");var subQ8=sQuery(id+"F0.wireOp",EDGE,"E1.top");var subQ9=sQuery(id+"F0.wireOp",EDGE,"E1.left");var subQ10=sQuery(id+"F0.wireOp",EDGE,"E23.filletArc");var subQ11=sQuery(id+"F0.wireOp",EDGE,"E24.filletArc");Q0=makeQuery(id+"F2.boolean.opBoolean","SPLIT",FACE,{"disambiguationData":[TD([makeQuery(id+"F1.opExtrude","SWEPT_FACE",FACE,{"disambiguationData":[OSD([subQ6])]})])],"derivedFrom":makeQuery(id+"F1.opExtrude","CAP_FACE",FACE,{"disambiguationData":[OSD([subQ6,subQ8,subQ9,subQ7,subQ4,subQ3,subQ2,subQ1,subQ0,subQ5,subQ10,subQ11])],"isStart":true})});}
            var sketch = newSketch(context, id + "F16", { "sketchPlane" : qUnion([Q0])});
            skPoint(sketch, "E79.centerSnap0", {"position": v(0, 90) * mm});
            skLineSegment(sketch, "E80", {"start": v(-15, 108) * mm, "end": v(-15, 120) * mm});
            skArc(sketch, "E81", {"start": v(15, 120) * mm, "mid": v(0, 135) * mm, "end": v(-15, 120) * mm});
            skCircle(sketch, "E82", {"center": v(0, 120) * mm, "radius": 6 * mm});
            skLineSegment(sketch, "E83", {"start": v(15, 120) * mm, "end": v(15, 108) * mm});
            skLineSegment(sketch, "E84", {"start": v(15, 108) * mm, "end": v(33, 90) * mm});
            skLineSegment(sketch, "E85", {"start": v(-15, 108) * mm, "end": v(-33, 90) * mm});
            skLineSegment(sketch, "E86", {"start": v(-80, 0) * mm, "end": v(80, 0) * mm, "construction": true});
            skLineSegment(sketch, "E87", {"start": v(0, 120) * mm, "end": v(0, 90) * mm, "construction": true});
            skLineSegment(sketch, "E88.MirrorCS", {"start": v(-15, -108) * mm, "end": v(-33, -90) * mm});
            skLineSegment(sketch, "E89.MirrorCS", {"start": v(-15, -108) * mm, "end": v(-15, -120) * mm});
            skArc(sketch, "E90.MirrorCS", {"start": v(15, -120) * mm, "mid": v(0, -135) * mm, "end": v(-15, -120) * mm});
            skCircle(sketch, "E91.MirrorC", {"center": v(0, -120) * mm, "radius": 6 * mm});
            skLineSegment(sketch, "E92.MirrorCS", {"start": v(0, -120) * mm, "end": v(0, -90) * mm, "construction": true});
            skLineSegment(sketch, "E93.MirrorCS", {"start": v(15, -120) * mm, "end": v(15, -108) * mm});
            skLineSegment(sketch, "E94.MirrorCS", {"start": v(15, -108) * mm, "end": v(33, -90) * mm});
            skSolve(sketch);
        }
        {
            var Q0;
            Q0=makeQuery(id+"F16.imprint","IMPRINT",FACE,{"disambiguationData":[TD([[makeQuery(id+"F16.imprint","IMPRINT",EDGE,{"derivedFrom":sQuery(id+"F16.wireOp",EDGE,"E80")}),-1.0]])]});
            var Q1;
            Q1=makeQuery(id+"F16.imprint","IMPRINT",FACE,{"disambiguationData":[TD([[makeQuery(id+"F16.imprint","IMPRINT",EDGE,{"derivedFrom":makeQuery(id+"F1.opExtrude","CAP_EDGE",EDGE,{"disambiguationData":[OSD([sQuery(id+"F0.wireOp",EDGE,"E1.left")])],"isStart":true})}),-1.0]])]});
            var Q2;
            {var subQ0=sQuery(id+"F16.wireOp",EDGE,"E88.MirrorCS");Q2=makeQuery(id+"F16.imprint","IMPRINT",FACE,{"disambiguationData":[TD([[makeQuery(id+"F16.imprint","IMPRINT",EDGE,{"derivedFrom":subQ0}),-1.0]])]});}
            var Q3;
            Q3=makeQuery(id+"F2.opExtrude","CAP_FACE",FACE,{"disambiguationData":[OSD([sQuery(id+"F0.wireOp",EDGE,"E12"),sQuery(id+"F0.wireOp",EDGE,"E13"),sQuery(id+"F0.wireOp",EDGE,"E14"),sQuery(id+"F0.wireOp",EDGE,"E15"),sQuery(id+"F0.wireOp",EDGE,"E17.filletArc"),sQuery(id+"F0.wireOp",EDGE,"E18.filletArc"),sQuery(id+"F0.wireOp",EDGE,"E19.filletArc"),sQuery(id+"F0.wireOp",EDGE,"E20.filletArc"),sQuery(id+"F0.wireOp",EDGE,"E25.0"),sQuery(id+"F0.wireOp",EDGE,"E25.1"),sQuery(id+"F0.wireOp",EDGE,"E25.2"),sQuery(id+"F0.wireOp",EDGE,"E25.3"),sQuery(id+"F0.wireOp",EDGE,"E25.4"),sQuery(id+"F0.wireOp",EDGE,"E25.5"),sQuery(id+"F0.wireOp",EDGE,"E25.6"),sQuery(id+"F0.wireOp",EDGE,"E25.7")])],"isStart":false});
            extrude(context, id + "F17", {"entities" : qUnion([Q0, Q1, Q2]), "endBound" : BoundingType.UP_TO_SURFACE, "endBoundEntityFace" : qUnion([Q3]), "depth" : 25 * mm});
        }
    });
